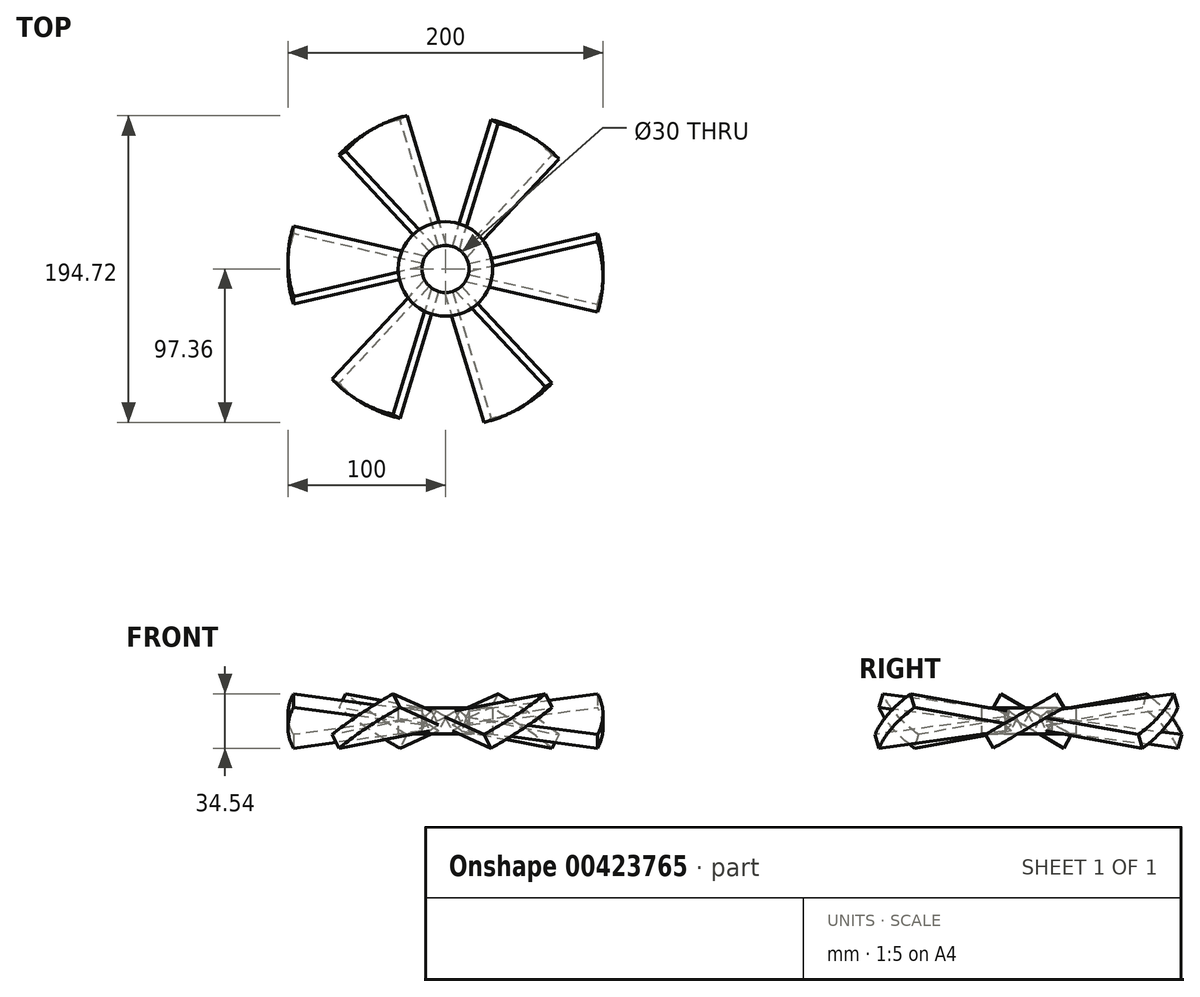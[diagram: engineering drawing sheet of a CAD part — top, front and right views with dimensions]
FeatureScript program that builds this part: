
annotation { "Feature Type Name" : "Feature", "Feature Type Description" : "" }
export const myFeature = defineFeature(function(context is Context, id is Id, definition is map)
    precondition{}
    {
        {
            var Q0;
            Q0=qCreatedBy(makeId("Top.planeOp"),FACE);
            var sketch = newSketch(context, id + "F0", { "sketchPlane" : qUnion([Q0])});
            skLineSegment(sketch, "E0", {"start": v(0, 0) * mm, "end": v(96.6, 25.88) * mm});
            skLineSegment(sketch, "E1", {"start": v(0, 0) * mm, "end": v(96.6, -25.88) * mm});
            skArc(sketch, "E2", {"start": v(96.6, -25.88) * mm, "mid": v(100, 0) * mm, "end": v(96.6, 25.88) * mm});
            skPoint(sketch, "E3.orphan", {"position": v(123.36, 33.05) * mm});
            skPoint(sketch, "E4.orphan", {"position": v(123.36, -33.05) * mm});
            skSolve(sketch);
        }
        {
            var Q0;
            Q0=makeQuery(id+"F0.imprint","IMPRINT",FACE,{"disambiguationData":[TD([[makeQuery(id+"F0.imprint","IMPRINT",EDGE,{"derivedFrom":sQuery(id+"F0.wireOp",EDGE,"E0")}),-1.0]])]});
            extrude(context, id + "F1", {"entities" : qUnion([Q0]), "depth" : 10 * mm});
        }
        {
            var Q0;
            Q0=qCreatedBy(makeId("Top.planeOp"),FACE);
            var sketch = newSketch(context, id + "F2", { "sketchPlane" : qUnion([Q0])});
            skLineSegment(sketch, "E5", {"start": v(0, 0) * mm, "end": v(110.51, 0) * mm});
            skSolve(sketch);
        }
        {
            var Q0;
            Q0=makeQuery(id+"F1.opExtrude","SWEPT_BODY",BODY,{"disambiguationData":[OSD([sQuery(id+"F0.wireOp",EDGE,"E0"),sQuery(id+"F0.wireOp",EDGE,"E1"),sQuery(id+"F0.wireOp",EDGE,"E2")])]});
            var Q1;
            Q1=sQuery(id+"F2.wireOp",EDGE,"E5");
            transform(context, id + "F3", {"entities" : qUnion([Q0]), "transformType" : TransformType.ROTATION, "transformAxis" : qUnion([Q1]), "angle" : 30 * degree, "makeCopy" : false});
        }
        {
            var Q0;
            Q0=qCreatedBy(makeId("Front.planeOp"),FACE);
            var sketch = newSketch(context, id + "F4", { "sketchPlane" : qUnion([Q0])});
            skLineSegment(sketch, "E6", {"start": v(0, 0) * mm, "end": v(0, 30.5) * mm});
            skSolve(sketch);
        }
        {
            var Q0;
            Q0=makeQuery(id+"F1.opExtrude","SWEPT_BODY",BODY,{"disambiguationData":[OSD([sQuery(id+"F0.wireOp",EDGE,"E0"),sQuery(id+"F0.wireOp",EDGE,"E1"),sQuery(id+"F0.wireOp",EDGE,"E2")])]});
            var Q1;
            Q1=sQuery(id+"F4.wireOp",EDGE,"E6");
            circularPattern(context, id + "F5", {"entities" : qUnion([Q0]), "axis" : qUnion([Q1]), "angle" : 360 * degree, "instanceCount" : 6, "equalSpace" : true});
        }
        {
            var Q0;
            Q0=qCreatedBy(makeId("Top.planeOp"),FACE);
            var sketch = newSketch(context, id + "F6", { "sketchPlane" : qUnion([Q0])});
            skCircle(sketch, "E7", {"center": v(0, 0) * mm, "radius": 30 * mm});
            skCircle(sketch, "E8", {"center": v(0, 0) * mm, "radius": 15 * mm});
            skSolve(sketch);
        }
        {
            var Q0;
            Q0 = qSketchRegion(id + "F6", true);
            extrude(context, id + "F7", {"entities" : qUnion([Q0]), "depth" : 12.8 * mm, "hasSecondDirection" : true, "secondDirectionOppositeDirection" : true, "secondDirectionDepth" : 4 * mm});
        }
        {
            var Q0;
            Q0=qCreatedBy(makeId("Top.planeOp"),FACE);
            var sketch = newSketch(context, id + "F8", { "sketchPlane" : qUnion([Q0])});
            skCircle(sketch, "E9", {"center": v(0, 0) * mm, "radius": 15 * mm});
            skSolve(sketch);
        }
        {
            var Q0;
            Q0 = qSketchRegion(id + "F8", true);
            extrude(context, id + "F9", {"entities" : qUnion([Q0]), "operationType" : NewBodyOperationType.REMOVE, "oppositeDirection" : true, "depth" : 25 * mm, "hasSecondDirection" : true, "secondDirectionOppositeDirection" : false, "secondDirectionDepth" : 25 * mm});
        }
    });
